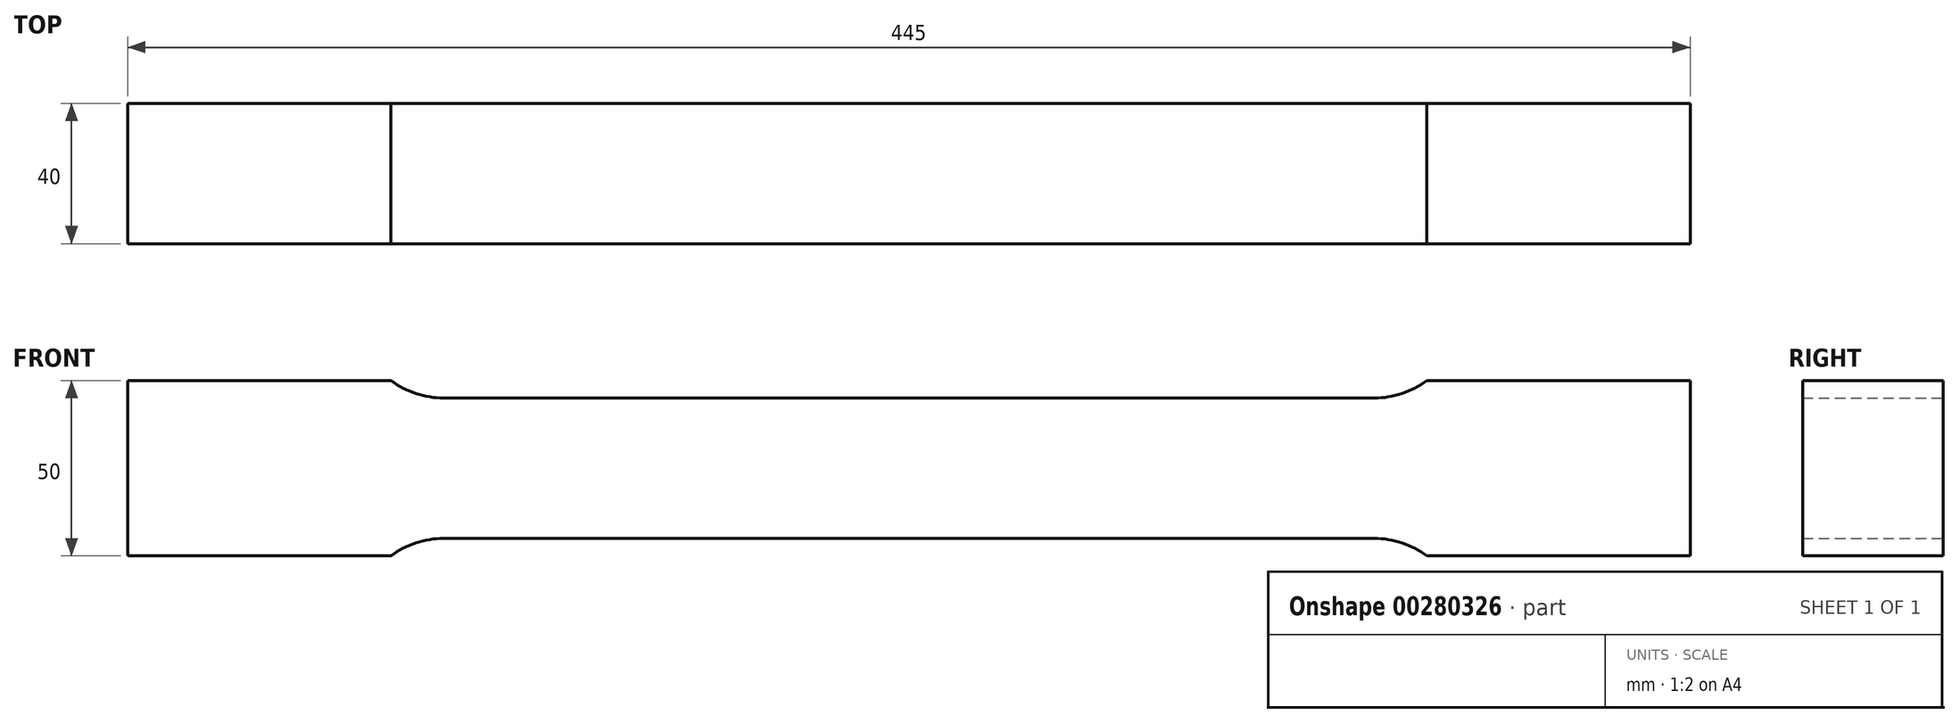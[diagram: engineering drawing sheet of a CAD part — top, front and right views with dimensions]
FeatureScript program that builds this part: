
annotation { "Feature Type Name" : "Feature", "Feature Type Description" : "" }
export const myFeature = defineFeature(function(context is Context, id is Id, definition is map)
    precondition{}
    {
        {
            var Q0;
            Q0=qCreatedBy(makeId("Front.planeOp"),FACE);
            var sketch = newSketch(context, id + "F0", { "sketchPlane" : qUnion([Q0])});
            skLineSegment(sketch, "E0", {"start": v(0, 20) * mm, "end": v(132.5, 20) * mm});
            skArc(sketch, "E1", {"start": v(132.5, 20) * mm, "mid": v(140.4, 21.28) * mm, "end": v(147.5, 25) * mm});
            skLineSegment(sketch, "E2", {"start": v(147.5, 25) * mm, "end": v(222.5, 25) * mm});
            skLineSegment(sketch, "E3", {"start": v(222.5, 25) * mm, "end": v(222.5, 0) * mm});
            skArc(sketch, "E4.MirrorCS", {"start": v(132.5, -20) * mm, "mid": v(140.4, -21.28) * mm, "end": v(147.5, -25) * mm});
            skLineSegment(sketch, "E5.MirrorCS", {"start": v(0, -20) * mm, "end": v(132.5, -20) * mm});
            skLineSegment(sketch, "E6.MirrorCS", {"start": v(147.5, -25) * mm, "end": v(222.5, -25) * mm});
            skLineSegment(sketch, "E7.MirrorCS", {"start": v(222.5, -25) * mm, "end": v(222.5, 0) * mm});
            skArc(sketch, "E8.MirrorCS", {"start": v(-132.5, -20) * mm, "mid": v(-140.4, -21.28) * mm, "end": v(-147.5, -25) * mm});
            skArc(sketch, "E9.MirrorCS", {"start": v(-132.5, 20) * mm, "mid": v(-140.4, 21.28) * mm, "end": v(-147.5, 25) * mm});
            skLineSegment(sketch, "E10.MirrorCS", {"start": v(-222.5, -25) * mm, "end": v(-222.5, 0) * mm});
            skLineSegment(sketch, "E11.MirrorCS", {"start": v(0, 20) * mm, "end": v(-132.5, 20) * mm});
            skLineSegment(sketch, "E12.MirrorCS", {"start": v(-147.5, -25) * mm, "end": v(-222.5, -25) * mm});
            skLineSegment(sketch, "E13.MirrorCS", {"start": v(0, -20) * mm, "end": v(-132.5, -20) * mm});
            skLineSegment(sketch, "E14.MirrorCS", {"start": v(-222.5, 25) * mm, "end": v(-222.5, 0) * mm});
            skLineSegment(sketch, "E15.MirrorCS", {"start": v(-147.5, 25) * mm, "end": v(-222.5, 25) * mm});
            skSolve(sketch);
        }
        {
            var Q0;
            Q0=makeQuery(id+"F0.imprint","IMPRINT",FACE,{"disambiguationData":[TD([[makeQuery(id+"F0.imprint","IMPRINT",EDGE,{"derivedFrom":sQuery(id+"F0.wireOp",EDGE,"E5.MirrorCS")}),1.0]])]});
            extrude(context, id + "F1", {"entities" : qUnion([Q0]), "endBound" : BoundingType.SYMMETRIC, "depth" : 40 * mm});
        }
    });
